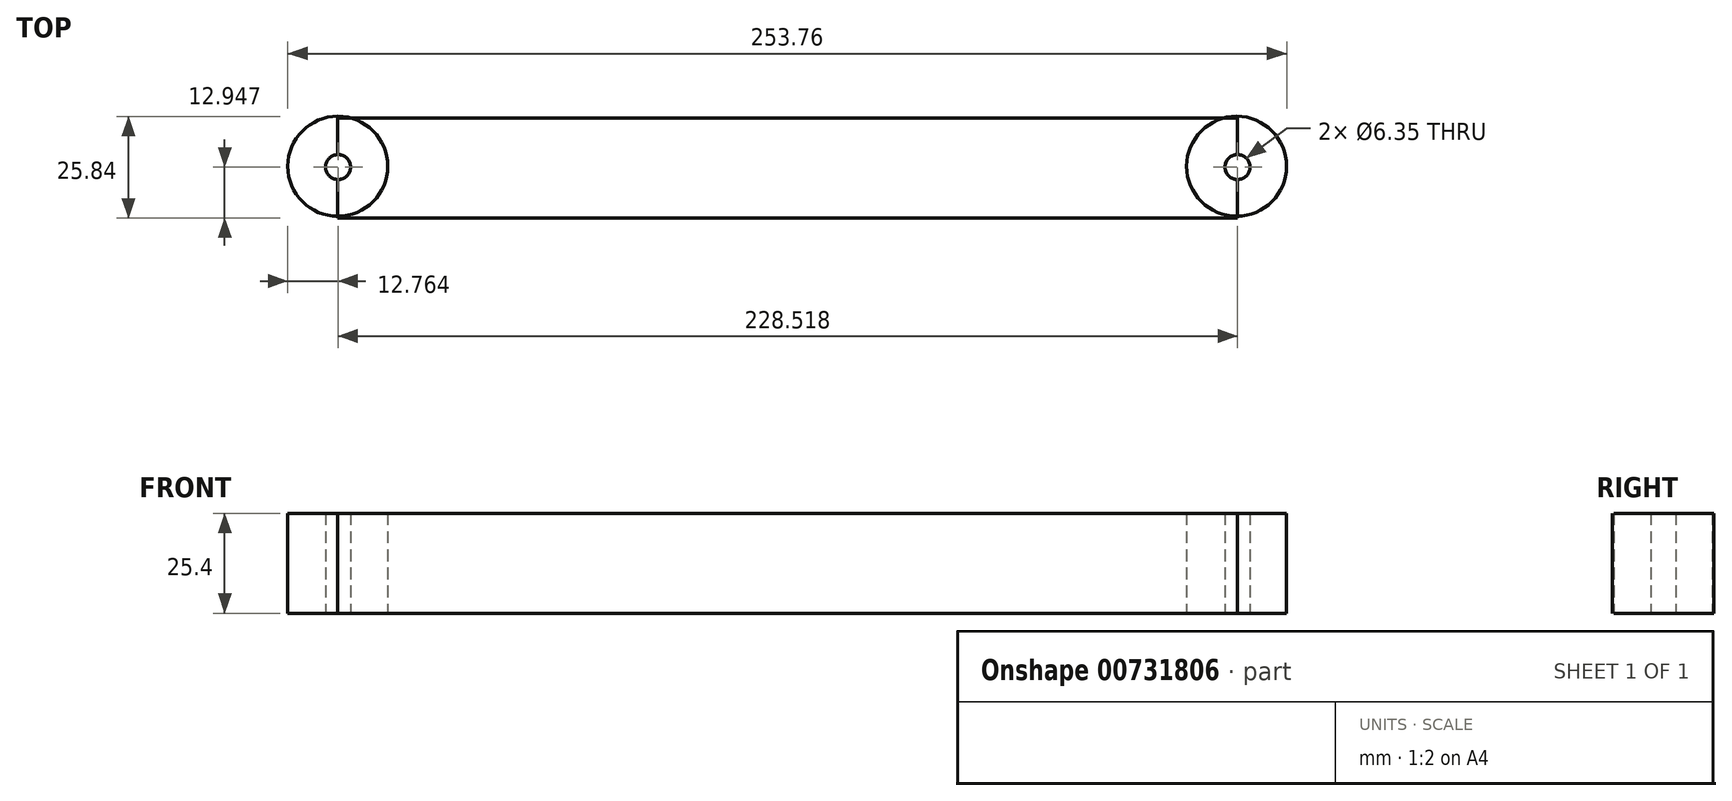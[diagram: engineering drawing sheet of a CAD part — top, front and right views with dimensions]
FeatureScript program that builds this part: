
annotation { "Feature Type Name" : "Feature", "Feature Type Description" : "" }
export const myFeature = defineFeature(function(context is Context, id is Id, definition is map)
    precondition{}
    {
        {
            var Q0;
            Q0=qCreatedBy(makeId("Top.planeOp"),FACE);
            var sketch = newSketch(context, id + "F0", { "sketchPlane" : qUnion([Q0])});
            skLineSegment(sketch, "E0", {"start": v(-70.36, -2.73) * mm, "end": v(158.24, -2.73) * mm});
            skLineSegment(sketch, "E1", {"start": v(158.24, -2.73) * mm, "end": v(158.24, 22.67) * mm});
            skLineSegment(sketch, "E2", {"start": v(158.24, 22.67) * mm, "end": v(-70.36, 22.67) * mm});
            skLineSegment(sketch, "E3", {"start": v(-70.36, 22.67) * mm, "end": v(-70.36, -2.73) * mm});
            skSolve(sketch);
        }
        {
            var Q0;
            Q0=qCreatedBy(makeId("Top.planeOp"),FACE);
            var sketch = newSketch(context, id + "F1", { "sketchPlane" : qUnion([Q0])});
            skCircle(sketch, "E4", {"center": v(-70.36, 10.41) * mm, "radius": 12.7 * mm});
            skCircle(sketch, "E5", {"center": v(158, 10.41) * mm, "radius": 12.7 * mm});
            skSolve(sketch);
        }
        {
            var Q0;
            Q0=makeQuery(id+"F1.imprint","IMPRINT",FACE,{"disambiguationData":[TD([[makeQuery(id+"F1.imprint","IMPRINT",EDGE,{"derivedFrom":sQuery(id+"F1.wireOp",EDGE,"E4")}),1.0]])]});
            var Q1;
            Q1=makeQuery(id+"F0.imprint","IMPRINT",FACE,{"disambiguationData":[TD([[makeQuery(id+"F0.imprint","IMPRINT",EDGE,{"derivedFrom":sQuery(id+"F0.wireOp",EDGE,"E0")}),1.0]])]});
            var Q2;
            Q2=makeQuery(id+"F1.imprint","IMPRINT",FACE,{"disambiguationData":[TD([[makeQuery(id+"F1.imprint","IMPRINT",EDGE,{"derivedFrom":sQuery(id+"F1.wireOp",EDGE,"E5")}),1.0]])]});
            extrude(context, id + "F2", {"entities" : qUnion([Q0, Q1, Q2]), "depth" : 25.4 * mm, "offsetDistance" : 25.4 * mm});
        }
        {
            var Q0;
            Q0=qCreatedBy(makeId("Top.planeOp"),FACE);
            var sketch = newSketch(context, id + "F3", { "sketchPlane" : qUnion([Q0])});
            skCircle(sketch, "E6", {"center": v(-70.3, 10.22) * mm, "radius": 12.7 * mm});
            skSolve(sketch);
        }
        {
            var Q0;
            Q0=sQuery(id+"F3.wireOp",VERTEX,"E6.center");
            var Q1;
            Q1=makeQuery(id+"F2.opExtrude","SWEPT_BODY",BODY,{"disambiguationData":[OSD([sQuery(id+"F0.wireOp",EDGE,"E0"),sQuery(id+"F0.wireOp",EDGE,"E1"),sQuery(id+"F0.wireOp",EDGE,"E2"),sQuery(id+"F0.wireOp",EDGE,"E3")])]});
            var Q2;
            Q2=makeQuery(id+"F2.opExtrude","SWEPT_BODY",BODY,{"disambiguationData":[OSD([sQuery(id+"F1.wireOp",EDGE,"E4")])]});
            hole(context, id + "F4", {"style" : HoleStyle.SIMPLE, "endStyle" : HoleEndStyle.THROUGH, "oppositeDirection" : true, "holeDiameter" : 6.35 * mm, "majorDiameter" : 6.35 * mm, "isTappedThrough" : true, "tappedDepth" : 12.7 * mm, "tapClearance" : 3, "locations" : qUnion([Q0]), "scope" : qUnion([Q1, Q2])});
        }
        {
            var Q0;
            Q0=qCreatedBy(makeId("Top.planeOp"),FACE);
            var sketch = newSketch(context, id + "F5", { "sketchPlane" : qUnion([Q0])});
            skCircle(sketch, "E7", {"center": v(158.22, 10.22) * mm, "radius": 12.7 * mm});
            skSolve(sketch);
        }
        {
            var Q0;
            Q0=sQuery(id+"F5.wireOp",VERTEX,"E7.center");
            var Q1;
            Q1=makeQuery(id+"F2.opExtrude","SWEPT_BODY",BODY,{"disambiguationData":[OSD([sQuery(id+"F0.wireOp",EDGE,"E0"),sQuery(id+"F0.wireOp",EDGE,"E1"),sQuery(id+"F0.wireOp",EDGE,"E2"),sQuery(id+"F0.wireOp",EDGE,"E3")])]});
            var Q2;
            Q2=makeQuery(id+"F2.opExtrude","SWEPT_BODY",BODY,{"disambiguationData":[OSD([sQuery(id+"F1.wireOp",EDGE,"E5")])]});
            hole(context, id + "F6", {"style" : HoleStyle.SIMPLE, "endStyle" : HoleEndStyle.THROUGH, "oppositeDirection" : true, "holeDiameter" : 6.35 * mm, "majorDiameter" : 6.35 * mm, "isTappedThrough" : true, "tappedDepth" : 12.7 * mm, "tapClearance" : 3, "locations" : qUnion([Q0]), "scope" : qUnion([Q1, Q2])});
        }
    });
